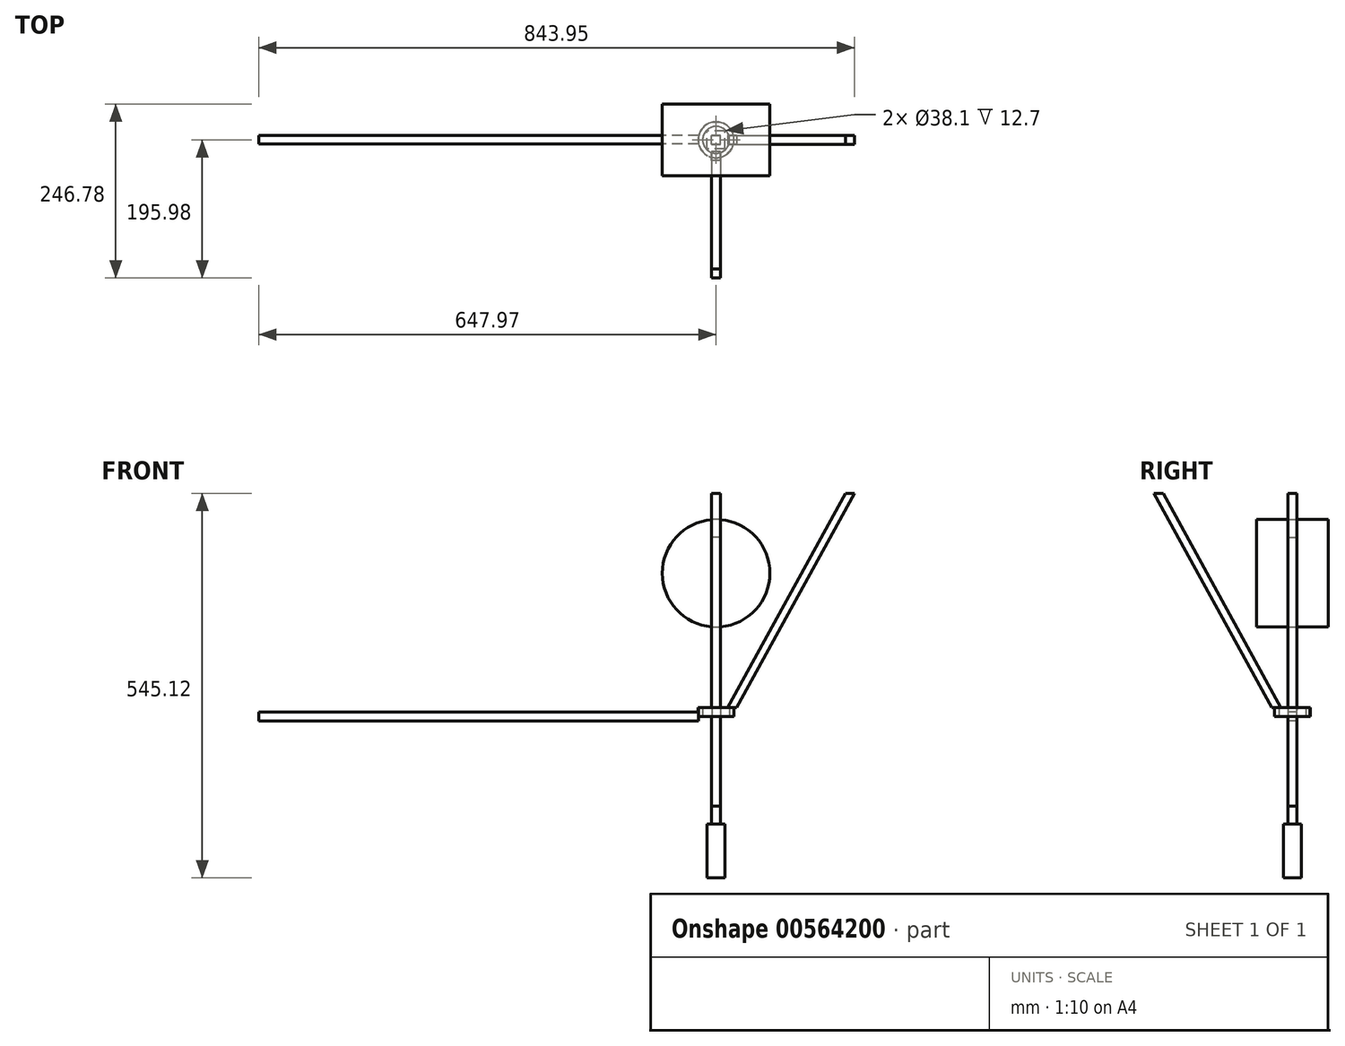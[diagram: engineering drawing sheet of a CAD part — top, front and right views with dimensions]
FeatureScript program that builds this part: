
annotation { "Feature Type Name" : "Feature", "Feature Type Description" : "" }
export const myFeature = defineFeature(function(context is Context, id is Id, definition is map)
    precondition{}
    {
        {
            var Q0;
            Q0=qCreatedBy(makeId("Front.planeOp"),FACE);
            var sketch = newSketch(context, id + "F0", { "sketchPlane" : qUnion([Q0])});
            skLineSegment(sketch, "E0.bottom", {"start": v(-6.35, 127) * mm, "end": v(6.35, 127) * mm});
            skLineSegment(sketch, "E0.top", {"start": v(-6.35, -127) * mm, "end": v(6.35, -127) * mm});
            skLineSegment(sketch, "E0.left", {"start": v(-6.35, 127) * mm, "end": v(-6.35, -127) * mm});
            skLineSegment(sketch, "E0.right", {"start": v(6.35, 127) * mm, "end": v(6.35, -127) * mm});
            skPoint(sketch, "E0.middle", {"position": v(0, 0) * mm});
            skSolve(sketch);
        }
        {
            var Q0;
            Q0=makeQuery(id+"F0.imprint","IMPRINT",FACE,{"disambiguationData":[TD([[makeQuery(id+"F0.imprint","IMPRINT",EDGE,{"derivedFrom":sQuery(id+"F0.wireOp",EDGE,"E0.bottom")}),-1.0]])]});
            extrude(context, id + "F1", {"entities" : qUnion([Q0]), "endBound" : BoundingType.SYMMETRIC, "depth" : 12.7 * mm, "offsetDistance" : 25.4 * mm});
        }
        {
            var Q0;
            Q0=qCreatedBy(makeId("Top.planeOp"),FACE);
            var sketch = newSketch(context, id + "F2", { "sketchPlane" : qUnion([Q0])});
            skCircle(sketch, "E1", {"center": v(0, 0) * mm, "radius": 19.05 * mm});
            skCircle(sketch, "E2", {"center": v(0, 0) * mm, "radius": 25.4 * mm});
            skLineSegment(sketch, "E3.bottom", {"start": v(-24.66, 6.07) * mm, "end": v(-647.97, 6.07) * mm});
            skLineSegment(sketch, "E3.top", {"start": v(-24.66, -6.07) * mm, "end": v(-647.97, -6.07) * mm});
            skLineSegment(sketch, "E3.left", {"start": v(-24.66, 6.07) * mm, "end": v(-24.66, -6.07) * mm});
            skLineSegment(sketch, "E3.right", {"start": v(-647.97, 6.07) * mm, "end": v(-647.97, -6.07) * mm});
            skPoint(sketch, "E3.middle", {"position": v(-336.32, 0) * mm});
            skSolve(sketch);
        }
        {
            var Q0;
            {var subQ1=sQuery(id+"F2.wireOp",EDGE,"E3.bottom");Q0=makeQuery(id+"F2.imprint","IMPRINT",FACE,{"disambiguationData":[TD([[makeQuery(id+"F2.imprint","IMPRINT",EDGE,{"derivedFrom":subQ1}),1.0]])]});}
            extrude(context, id + "F3", {"entities" : qUnion([Q0]), "endBound" : BoundingType.SYMMETRIC, "depth" : 12.7 * mm, "offsetDistance" : 25.4 * mm});
        }
        {
            var Q0;
            Q0=makeQuery(id+"F2.imprint","IMPRINT",FACE,{"disambiguationData":[TD([[makeQuery(id+"F2.imprint","IMPRINT",EDGE,{"derivedFrom":sQuery(id+"F2.wireOp",EDGE,"E1")}),-1.0]])]});
            extrude(context, id + "F4", {"entities" : qUnion([Q0]), "depth" : 12.7 * mm, "offsetDistance" : 25.4 * mm});
        }
        {
            var Q0;
            Q0=makeQuery(id+"F4.opExtrude","CAP_FACE",FACE,{"disambiguationData":[OSD([sQuery(id+"F2.wireOp",EDGE,"E1"),sQuery(id+"F2.wireOp",EDGE,"E2"),sQuery(id+"F2.wireOp",EDGE,"E3.left")])],"isStart":false});
            var sketch = newSketch(context, id + "F5", { "sketchPlane" : qUnion([Q0])});
            skLineSegment(sketch, "E4.bottom", {"start": v(29.34, 6.35) * mm, "end": v(16.38, 6.35) * mm});
            skLineSegment(sketch, "E4.top", {"start": v(29.34, -6.35) * mm, "end": v(16.38, -6.35) * mm});
            skLineSegment(sketch, "E4.left", {"start": v(29.34, 6.35) * mm, "end": v(29.34, -6.35) * mm});
            skLineSegment(sketch, "E4.right", {"start": v(16.38, 6.35) * mm, "end": v(16.38, -6.35) * mm});
            skPoint(sketch, "E4.middle", {"position": v(22.86, 0) * mm});
            skSolve(sketch);
        }
        {
            var Q0;
            Q0=qCreatedBy(makeId("Front.planeOp"),FACE);
            var sketch = newSketch(context, id + "F6", { "sketchPlane" : qUnion([Q0])});
            skLineSegment(sketch, "E5", {"start": v(189.5, 316.52) * mm, "end": v(22.86, 12.7) * mm});
            skSolve(sketch);
        }
        {
            var Q0;
            Q0 = qSketchRegion(id + "F5", true);
            var Q1;
            Q1=sQuery(id+"F6.wireOp",EDGE,"E5");
            sweep(context, id + "F7", {"operationType" : NewBodyOperationType.ADD, "profiles" : qUnion([Q0]), "path" : qUnion([Q1])});
        }
        {
            var Q0;
            Q0=qCreatedBy(makeId("Front.planeOp"),FACE);
            var sketch = newSketch(context, id + "F8", { "sketchPlane" : qUnion([Q0])});
            skCircle(sketch, "E6", {"center": v(0, 203.2) * mm, "radius": 76.2 * mm});
            skSolve(sketch);
        }
        {
            var Q0;
            Q0=makeQuery(id+"F8.imprint","IMPRINT",FACE,{"disambiguationData":[TD([[makeQuery(id+"F8.imprint","IMPRINT",EDGE,{"derivedFrom":sQuery(id+"F8.wireOp",EDGE,"E6")}),1.0]])]});
            var Q1;
            Q1 = qConstructionFilter(qBodyType(qCreatedBy(id + "F8" ,EDGE), BodyType.WIRE), ConstructionObject.NO);
            extrude(context, id + "F9", {"entities" : qUnion([Q0]), "operationType" : NewBodyOperationType.ADD, "surfaceEntities" : qUnion([Q1]), "endBound" : BoundingType.SYMMETRIC, "depth" : 101.6 * mm, "offsetDistance" : 25.4 * mm});
        }
        {
            var Q0;
            Q0=makeQuery(id+"F1.opExtrude","SWEPT_FACE",FACE,{"disambiguationData":[OSD([sQuery(id+"F0.wireOp",EDGE,"E0.top")])]});
            cPlane(context, id + "F10", {"entities" : qUnion([Q0]), "cplaneType" : CPlaneType.OFFSET, "offset" : 25.4 * mm, "width" : 152.4 * mm, "height" : 152.4 * mm});
        }
        {
            var Q0;
            Q0=qCreatedBy(id+"F10.planeOp",FACE);
            var sketch = newSketch(context, id + "F11", { "sketchPlane" : qUnion([Q0])});
            skLineSegment(sketch, "E7.bottom", {"start": v(6.35, 6.31) * mm, "end": v(-6.35, 6.31) * mm});
            skLineSegment(sketch, "E7.top", {"start": v(6.35, -6.31) * mm, "end": v(-6.35, -6.31) * mm});
            skLineSegment(sketch, "E7.left", {"start": v(6.35, 6.31) * mm, "end": v(6.35, -6.31) * mm});
            skLineSegment(sketch, "E7.right", {"start": v(-6.35, 6.31) * mm, "end": v(-6.35, -6.31) * mm});
            skPoint(sketch, "E7.middle", {"position": v(0, 0) * mm});
            skSolve(sketch);
        }
        {
            var Q0;
            Q0 = qSketchRegion(id + "F11", true);
            extrude(context, id + "F12", {"entities" : qUnion([Q0]), "oppositeDirection" : true, "depth" : 406.4 * mm, "offsetDistance" : 25.4 * mm});
        }
        {
            var Q0;
            Q0=qCreatedBy(id+"F10.planeOp",FACE);
            var sketch = newSketch(context, id + "F13", { "sketchPlane" : qUnion([Q0])});
            skLineSegment(sketch, "E8.bottom", {"start": v(12.7, 12.8) * mm, "end": v(-12.7, 12.8) * mm});
            skLineSegment(sketch, "E8.top", {"start": v(12.7, -12.8) * mm, "end": v(-12.7, -12.8) * mm});
            skLineSegment(sketch, "E8.left", {"start": v(12.7, 12.8) * mm, "end": v(12.7, -12.8) * mm});
            skLineSegment(sketch, "E8.right", {"start": v(-12.7, 12.8) * mm, "end": v(-12.7, -12.8) * mm});
            skPoint(sketch, "E8.middle", {"position": v(0, 0) * mm});
            skSolve(sketch);
        }
        {
            var Q0;
            Q0=makeQuery(id+"F13.imprint","IMPRINT",FACE,{"disambiguationData":[TD([[makeQuery(id+"F13.imprint","IMPRINT",EDGE,{"derivedFrom":sQuery(id+"F13.wireOp",EDGE,"E8.bottom")}),1.0]])]});
            extrude(context, id + "F14", {"entities" : qUnion([Q0]), "operationType" : NewBodyOperationType.ADD, "depth" : 76.2 * mm, "offsetDistance" : 25.4 * mm});
        }
        {
            var Q0;
            Q0=makeQuery(id+"F4.opExtrude","SWEPT_BODY",BODY,{"disambiguationData":[OSD([sQuery(id+"F2.wireOp",EDGE,"E1"),sQuery(id+"F2.wireOp",EDGE,"E2"),sQuery(id+"F2.wireOp",EDGE,"E3.left")])]});
            var Q1;
            Q1=makeQuery(id+"F4.opExtrude","SWEPT_FACE",FACE,{"disambiguationData":[OSD([sQuery(id+"F2.wireOp",EDGE,"E2")])]});
            circularPattern(context, id + "F15", {"entities" : qUnion([Q0]), "axis" : qUnion([Q1]), "angle" : 90 * degree, "instanceCount" : 2, "equalSpace" : true});
        }
    });
